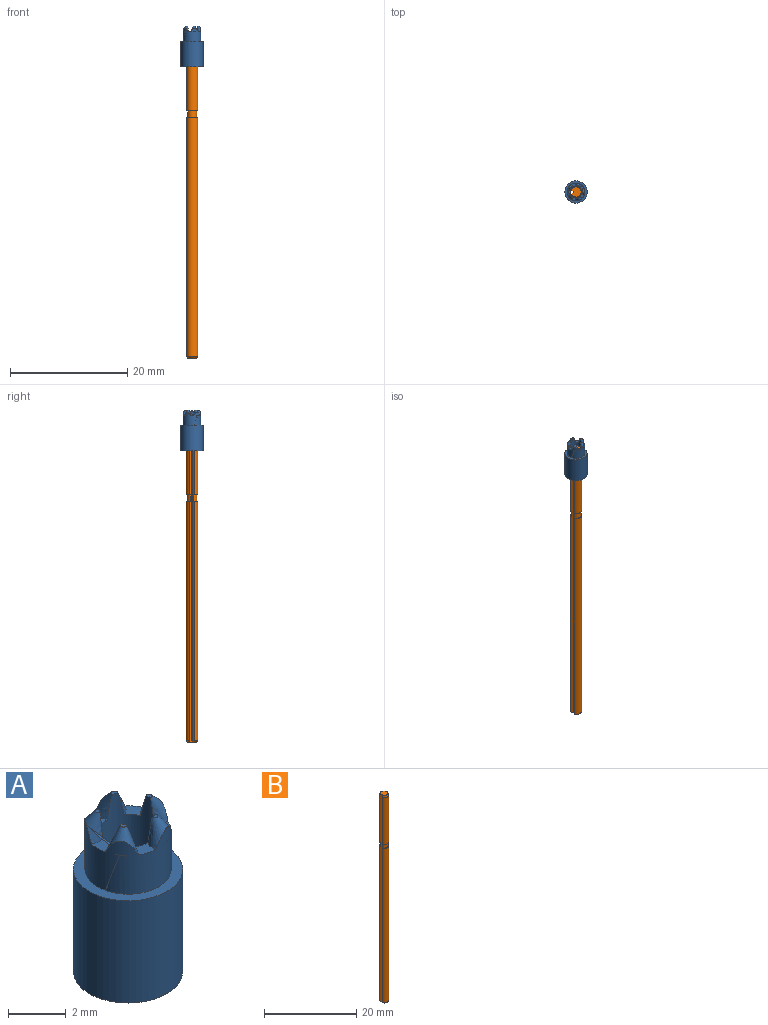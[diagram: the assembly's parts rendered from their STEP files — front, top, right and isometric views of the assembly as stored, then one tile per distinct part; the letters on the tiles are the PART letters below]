
ASSEMBLY  parts=2 mates=1
PART A: 30 faces, bbox 3.9x3.9x7.1 mm
  f0: plane 0.39x0.02mm, normal (0.34,0,-0.94), area 0mm2, adj f4,f5
  f1: cone r=0.6mm half-angle=24.8deg, axis (0.34,0,-0.94), area 1mm2, adj f2,f3,f4,f6,f26
  f2: plane 0.34x0.27mm, normal (0,0,1), area 0mm2, adj f1,f3
  f3: cylinder r=1mm len=6.95mm, axis (0,0,-1), area 39.8mm2, adj f1,f2,f6,f7,f9,f11,f12,f14
  f4: cylinder r=1.5mm len=3mm, axis (0,0,-1), area 17.9mm2, adj f0,f1,f5,f6,f8,f9,f10,f11
  f5: plane 0.38x0.01mm, normal (0,0,1), area 0mm2, adj f0,f4
  f6: plane 0.83x0.8mm, normal (0,0,1), area 0.3mm2, adj f1,f3,f4,f9
  f7: plane 0.34x0.3mm, normal (0,0,1), area 0mm2, adj f3,f9
  f8: plane 0.37x0.13mm, normal (0.11,0.33,-0.94), area 0mm2, adj f4,f10
  f9: cone r=0.6mm half-angle=24.8deg, axis (0.11,0.33,-0.94), area 1mm2, adj f3,f4,f6,f7,f11
  f10: plane 0.37x0.12mm, normal (0,0,1), area 0mm2, adj f4,f8
  f11: plane 0.78x0.7mm, normal (0,0,1), area 0.3mm2, adj f3,f4,f9,f14
  f12: plane 0.34x0.32mm, normal (0,0,1), area 0mm2, adj f3,f14
  f13: plane 0.32x0.23mm, normal (-0.28,0.2,-0.94), area 0mm2, adj f4,f15
  f14: cone r=0.6mm half-angle=24.8deg, axis (-0.28,0.2,-0.94), area 1mm2, adj f3,f4,f11,f12,f16
  f15: plane 0.31x0.23mm, normal (0,0,1), area 0mm2, adj f4,f13
  f16: plane 0.71x0.57mm, normal (0,0,1), area 0.3mm2, adj f3,f4,f14,f19
  f17: plane 0.34x0.32mm, normal (0,0,1), area 0mm2, adj f3,f19
  f18: plane 0.32x0.23mm, normal (-0.28,-0.2,-0.94), area 0mm2, adj f4,f20
  f19: cone r=0.6mm half-angle=24.8deg, axis (-0.28,-0.2,-0.94), area 1mm2, adj f3,f4,f16,f17,f21
  f20: plane 0.31x0.23mm, normal (0,0,1), area 0mm2, adj f4,f18
  f21: plane 0.78x0.7mm, normal (0,0,1), area 0.3mm2, adj f3,f4,f19,f23
  f22: plane 0.37x0.13mm, normal (0.11,-0.33,-0.94), area 0mm2, adj f4,f25
  f23: cone r=0.6mm half-angle=24.8deg, axis (0.11,-0.33,-0.94), area 1mm2, adj f3,f4,f21,f24,f26
  f24: plane 0.34x0.3mm, normal (0,0,1), area 0mm2, adj f3,f23
  f25: plane 0.37x0.12mm, normal (0,0,1), area 0mm2, adj f4,f22
  f26: plane 0.83x0.8mm, normal (0,0,1), area 0.3mm2, adj f1,f3,f4,f23
  f27: cylinder r=1.9mm len=4.35mm, axis (0,0,1), area 51.9mm2, adj f28,f29
  f28: plane 3.8x3.8mm, normal (0,0,-1), area 8.2mm2, adj f3,f27
  f29: plane 3.8x3.8mm, normal (0,0,1), area 4.3mm2, adj f4,f27
PART B: 12 faces, bbox 1.9x2x55 mm
  f0: cylinder r=1mm len=40.85mm, axis (0,0,-1), area 215.9mm2, adj f2,f4,f7,f11
  f1: cylinder r=0.1mm len=55mm, axis (0,0,-1), area 8.6mm2, adj f2,f4,f5,f6
  f2: plane 55.01x0.42mm, normal (-0.71,0.71,0), area 31.4mm2, adj f0,f1,f3,f5,f6,f7,f8,f9
  f3: cylinder r=1mm len=12.35mm, axis (0,0,-1), area 65.3mm2, adj f2,f4,f8,f10
  f4: plane 55.01x0.42mm, normal (-0.71,-0.71,0), area 31.4mm2, adj f0,f1,f3,f5,f6,f7,f8,f9
  f5: plane 1.73x1.65mm, normal (0,0,1), area 2.2mm2, adj f1,f2,f4,f8
  f6: plane 1.6x1.53mm, normal (0,0,-1), area 1.9mm2, adj f1,f2,f4,f7
  f7: cone r=1mm half-angle=45deg, axis (0,0,1), area 1.4mm2, adj f0,f2,f4,f6
  f8: cone r=0.87mm half-angle=15deg, axis (0,0,-1), area 2.6mm2, adj f2,f3,f4,f5
  f9: cylinder r=0.8mm len=1.6mm, axis (0,0,-1), area 4.8mm2, adj f2,f4,f10,f11
  f10: plane 2x1.88mm, normal (0,0,-1), area 1mm2, adj f2,f3,f4,f9
  f11: plane 2x1.88mm, normal (0,0,1), area 1mm2, adj f0,f2,f4,f9
PLACE A at identity fixed
PLACE B t=(0,0,-54.05)mm
MATE fastened B.f0 <-> A.f3  axis (0,0,1) through (0,0,0.95)mm
